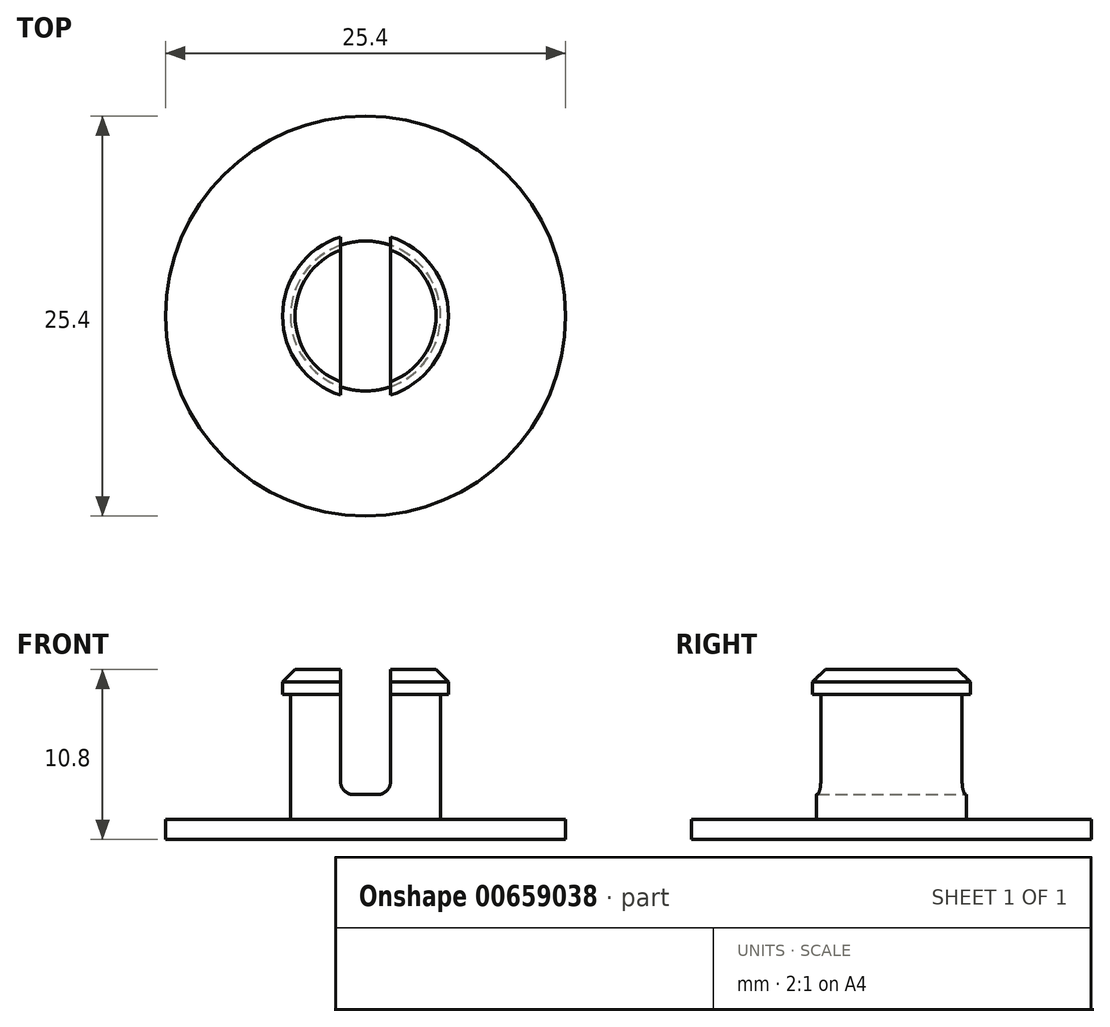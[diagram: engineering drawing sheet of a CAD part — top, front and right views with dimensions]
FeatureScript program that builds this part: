
annotation { "Feature Type Name" : "Feature", "Feature Type Description" : "" }
export const myFeature = defineFeature(function(context is Context, id is Id, definition is map)
    precondition{}
    {
        {
            var Q0;
            Q0=qCreatedBy(makeId("Front.planeOp"),FACE);
            var sketch = newSketch(context, id + "F0", { "sketchPlane" : qUnion([Q0])});
            skLineSegment(sketch, "E0.bottom", {"start": v(4.76, 0) * mm, "end": v(12.7, 0) * mm});
            skLineSegment(sketch, "E0.top", {"start": v(0, -1.27) * mm, "end": v(12.7, -1.27) * mm});
            skLineSegment(sketch, "E0.left", {"start": v(0, 0) * mm, "end": v(0, -1.27) * mm});
            skLineSegment(sketch, "E0.right", {"start": v(12.7, 0) * mm, "end": v(12.7, -1.27) * mm});
            skLineSegment(sketch, "E1.left", {"start": v(0, 0) * mm, "end": v(0, 7.94) * mm});
            skLineSegment(sketch, "E1.right", {"start": v(4.76, 0) * mm, "end": v(4.76, 7.94) * mm});
            skLineSegment(sketch, "E2.bottom", {"start": v(4.76, 7.94) * mm, "end": v(5.27, 7.94) * mm});
            skLineSegment(sketch, "E2.top", {"start": v(0, 9.52) * mm, "end": v(5.27, 9.52) * mm});
            skLineSegment(sketch, "E2.left", {"start": v(0, 7.94) * mm, "end": v(0, 9.52) * mm});
            skLineSegment(sketch, "E2.right", {"start": v(5.27, 7.94) * mm, "end": v(5.27, 9.52) * mm});
            skSolve(sketch);
        }
        {
            var Q0;
            Q0 = qSketchRegion(id + "F0", true);
            var Q1;
            Q1=sQuery(id+"F0.wireOp",EDGE,"E1.left");
            revolve(context, id + "F1", {"entities" : qUnion([Q0]), "axis" : qUnion([Q1]), "revolveType" : RevolveType.FULL});
        }
        {
            var Q0;
            Q0=makeQuery(id+"F1.opRevolve","SWEPT_EDGE",EDGE,{"disambiguationData":[OSD([sQuery(id+"F0.wireOp",EDGE,"E2.top"),sQuery(id+"F0.wireOp",EDGE,"E2.right")])]});
            chamfer(context, id + "F2", {"entities" : qUnion([Q0]), "width" : 0.8 * mm, "tangentPropagation" : true});
        }
        {
            var Q0;
            Q0=qCreatedBy(makeId("Front.planeOp"),FACE);
            var sketch = newSketch(context, id + "F3", { "sketchPlane" : qUnion([Q0])});
            skLineSegment(sketch, "E3.left", {"start": v(-1.59, 1.59) * mm, "end": v(-1.59, 9.52) * mm});
            skLineSegment(sketch, "E3.right", {"start": v(1.59, 1.59) * mm, "end": v(1.59, 9.52) * mm});
            skLineSegment(sketch, "E4.0", {"start": v(-1.59, 9.52) * mm, "end": v(1.59, 9.52) * mm});
            skLineSegment(sketch, "E5", {"start": v(-1.59, 1.59) * mm, "end": v(1.59, 1.59) * mm});
            skLineSegment(sketch, "E6", {"start": v(0, 0) * mm, "end": v(0, 1.59) * mm, "construction": true});
            skSolve(sketch);
        }
        {
            var Q0;
            Q0 = qSketchRegion(id + "F3", true);
            extrude(context, id + "F4", {"entities" : qUnion([Q0]), "operationType" : NewBodyOperationType.REMOVE, "endBound" : BoundingType.THROUGH_ALL, "depth" : 25.4 * mm, "offsetDistance" : 25.4 * mm, "hasSecondDirection" : true, "secondDirectionBound" : SecondDirectionBoundingType.THROUGH_ALL, "secondDirectionOppositeDirection" : true, "secondDirectionDepth" : 25.4 * mm});
        }
        {
            var Q0;
            Q0=makeQuery(id+"F4.boolean.opBoolean","COPY",EDGE,{"derivedFrom":makeQuery(id+"F4.opExtrude","SWEPT_EDGE",EDGE,{"disambiguationData":[OSD([sQuery(id+"F3.wireOp",EDGE,"E3.right"),sQuery(id+"F3.wireOp",EDGE,"E5")])]})});
            var Q1;
            Q1=makeQuery(id+"F4.boolean.opBoolean","COPY",EDGE,{"derivedFrom":makeQuery(id+"F4.opExtrude","SWEPT_EDGE",EDGE,{"disambiguationData":[OSD([sQuery(id+"F3.wireOp",EDGE,"E3.left"),sQuery(id+"F3.wireOp",EDGE,"E5")])]})});
            fillet(context, id + "F5", {"entities" : qUnion([Q0, Q1]), "radius" : 0.8 * mm, "tangentPropagation" : true, "allowEdgeOverflow" : false});
        }
    });
